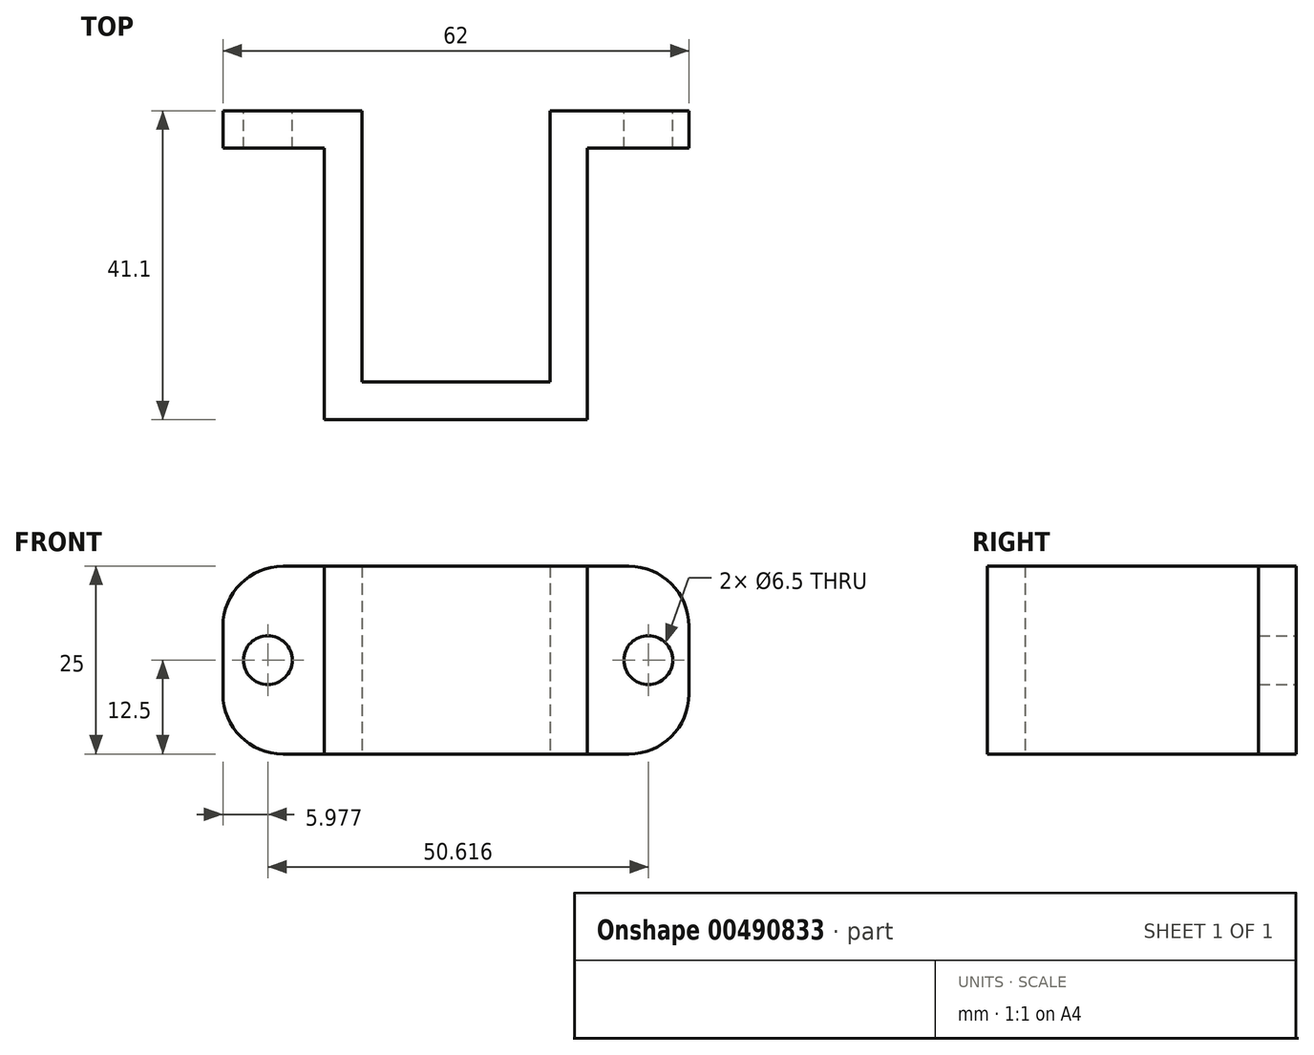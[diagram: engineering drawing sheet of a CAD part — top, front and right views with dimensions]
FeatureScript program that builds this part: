
annotation { "Feature Type Name" : "Feature", "Feature Type Description" : "" }
export const myFeature = defineFeature(function(context is Context, id is Id, definition is map)
    precondition{}
    {
        {
            var Q0;
            Q0=qCreatedBy(makeId("Top.planeOp"),FACE);
            var sketch = newSketch(context, id + "F0", { "sketchPlane" : qUnion([Q0])});
            skLineSegment(sketch, "E0", {"start": v(31, 32.85) * mm, "end": v(31, 27.85) * mm});
            skLineSegment(sketch, "E1", {"start": v(0, -8.25) * mm, "end": v(17.5, -8.25) * mm});
            skLineSegment(sketch, "E2", {"start": v(17.5, -8.25) * mm, "end": v(17.5, 27.85) * mm});
            skLineSegment(sketch, "E3", {"start": v(17.5, 27.85) * mm, "end": v(31, 27.85) * mm});
            skLineSegment(sketch, "E4", {"start": v(0, -3.25) * mm, "end": v(12.5, -3.25) * mm});
            skLineSegment(sketch, "E5", {"start": v(12.5, -3.25) * mm, "end": v(12.5, 32.85) * mm});
            skLineSegment(sketch, "E6.trimOffspring", {"start": v(12.5, 32.85) * mm, "end": v(31, 32.85) * mm});
            skPoint(sketch, "E7.start.orphan", {"position": v(-16.73, 27.85) * mm});
            skLineSegment(sketch, "E8.MirrorCS", {"start": v(-17.5, 27.85) * mm, "end": v(-31, 27.85) * mm});
            skLineSegment(sketch, "E9.MirrorCS", {"start": v(-17.5, -8.25) * mm, "end": v(-17.5, 27.85) * mm});
            skLineSegment(sketch, "E10.MirrorCS", {"start": v(-31, 32.85) * mm, "end": v(-31, 27.85) * mm});
            skLineSegment(sketch, "E11.MirrorCS", {"start": v(0, -3.25) * mm, "end": v(-12.5, -3.25) * mm});
            skLineSegment(sketch, "E12.MirrorCS", {"start": v(-12.5, -3.25) * mm, "end": v(-12.5, 32.85) * mm});
            skLineSegment(sketch, "E13.MirrorCS", {"start": v(-12.5, 32.85) * mm, "end": v(-31, 32.85) * mm});
            skLineSegment(sketch, "E14.MirrorCS", {"start": v(0, -8.25) * mm, "end": v(-17.5, -8.25) * mm});
            skPoint(sketch, "E15.MirrorP", {"position": v(16.73, 27.85) * mm});
            skPoint(sketch, "E16", {"position": v(-25.55, 32.85) * mm});
            skPoint(sketch, "E17.MirrorP", {"position": v(25.55, 32.85) * mm});
            skSolve(sketch);
        }
        {
            var Q0;
            Q0=makeQuery(id+"F0.imprint","IMPRINT",FACE,{"disambiguationData":[TD([[makeQuery(id+"F0.imprint","IMPRINT",EDGE,{"derivedFrom":sQuery(id+"F0.wireOp",EDGE,"E0")}),-1.0]])]});
            extrude(context, id + "F1", {"entities" : qUnion([Q0]), "depth" : 25 * mm, "offsetDistance" : 25 * mm});
        }
        {
            var Q0;
            Q0=makeQuery(id+"F1.opExtrude","SWEPT_FACE",FACE,{"disambiguationData":[OSD([sQuery(id+"F0.wireOp",EDGE,"E13.MirrorCS")])]});
            var sketch = newSketch(context, id + "F2", { "sketchPlane" : qUnion([Q0])});
            skCircle(sketch, "E18", {"center": v(25.02, 12.5) * mm, "radius": 1.5 * mm});
            skCircle(sketch, "E19", {"center": v(-25.6, 12.5) * mm, "radius": 1.5 * mm});
            skSolve(sketch);
        }
        {
            var Q0;
            Q0=sQuery(id+"F2.wireOp",VERTEX,"E18.center");
            var Q1;
            Q1=makeQuery(id+"F1.opExtrude","SWEPT_BODY",BODY,{"disambiguationData":[OSD([sQuery(id+"F0.wireOp",EDGE,"E0"),sQuery(id+"F0.wireOp",EDGE,"E1"),sQuery(id+"F0.wireOp",EDGE,"E2"),sQuery(id+"F0.wireOp",EDGE,"E3"),sQuery(id+"F0.wireOp",EDGE,"E4"),sQuery(id+"F0.wireOp",EDGE,"E5"),sQuery(id+"F0.wireOp",EDGE,"E6.trimOffspring"),sQuery(id+"F0.wireOp",EDGE,"E8.MirrorCS"),sQuery(id+"F0.wireOp",EDGE,"E9.MirrorCS"),sQuery(id+"F0.wireOp",EDGE,"E10.MirrorCS"),sQuery(id+"F0.wireOp",EDGE,"E11.MirrorCS"),sQuery(id+"F0.wireOp",EDGE,"E12.MirrorCS"),sQuery(id+"F0.wireOp",EDGE,"E13.MirrorCS"),sQuery(id+"F0.wireOp",EDGE,"E14.MirrorCS")])]});
            hole(context, id + "F3", {"style" : HoleStyle.SIMPLE, "endStyle" : HoleEndStyle.THROUGH, "holeDiameter" : 6.5 * mm, "isTappedThrough" : true, "tappedDepth" : 12 * mm, "tapClearance" : 3, "locations" : qUnion([Q0]), "scope" : qUnion([Q1])});
        }
        {
            var Q0;
            Q0=sQuery(id+"F2.wireOp",VERTEX,"E19.center");
            var Q1;
            Q1=makeQuery(id+"F1.opExtrude","SWEPT_BODY",BODY,{"disambiguationData":[OSD([sQuery(id+"F0.wireOp",EDGE,"E0"),sQuery(id+"F0.wireOp",EDGE,"E1"),sQuery(id+"F0.wireOp",EDGE,"E2"),sQuery(id+"F0.wireOp",EDGE,"E3"),sQuery(id+"F0.wireOp",EDGE,"E4"),sQuery(id+"F0.wireOp",EDGE,"E5"),sQuery(id+"F0.wireOp",EDGE,"E6.trimOffspring"),sQuery(id+"F0.wireOp",EDGE,"E8.MirrorCS"),sQuery(id+"F0.wireOp",EDGE,"E9.MirrorCS"),sQuery(id+"F0.wireOp",EDGE,"E10.MirrorCS"),sQuery(id+"F0.wireOp",EDGE,"E11.MirrorCS"),sQuery(id+"F0.wireOp",EDGE,"E12.MirrorCS"),sQuery(id+"F0.wireOp",EDGE,"E13.MirrorCS"),sQuery(id+"F0.wireOp",EDGE,"E14.MirrorCS")])]});
            hole(context, id + "F4", {"style" : HoleStyle.SIMPLE, "endStyle" : HoleEndStyle.THROUGH, "holeDiameter" : 6.5 * mm, "isTappedThrough" : true, "tappedDepth" : 12 * mm, "tapClearance" : 3, "locations" : qUnion([Q0]), "scope" : qUnion([Q1])});
        }
        {
            var Q0;
            Q0=makeQuery(id+"F1.opExtrude","CAP_EDGE",EDGE,{"disambiguationData":[OSD([sQuery(id+"F0.wireOp",EDGE,"E10.MirrorCS")])],"isStart":false});
            var Q1;
            Q1=makeQuery(id+"F1.opExtrude","CAP_EDGE",EDGE,{"disambiguationData":[OSD([sQuery(id+"F0.wireOp",EDGE,"E10.MirrorCS")])],"isStart":true});
            var Q2;
            Q2=makeQuery(id+"F1.opExtrude","CAP_EDGE",EDGE,{"disambiguationData":[OSD([sQuery(id+"F0.wireOp",EDGE,"E0")])],"isStart":false});
            var Q3;
            Q3=makeQuery(id+"F1.opExtrude","CAP_EDGE",EDGE,{"disambiguationData":[OSD([sQuery(id+"F0.wireOp",EDGE,"E0")])],"isStart":true});
            fillet(context, id + "F5", {"entities" : qUnion([Q0, Q1, Q2, Q3]), "radius" : 8 * mm, "tangentPropagation" : true, "allowEdgeOverflow" : false});
        }
    });
